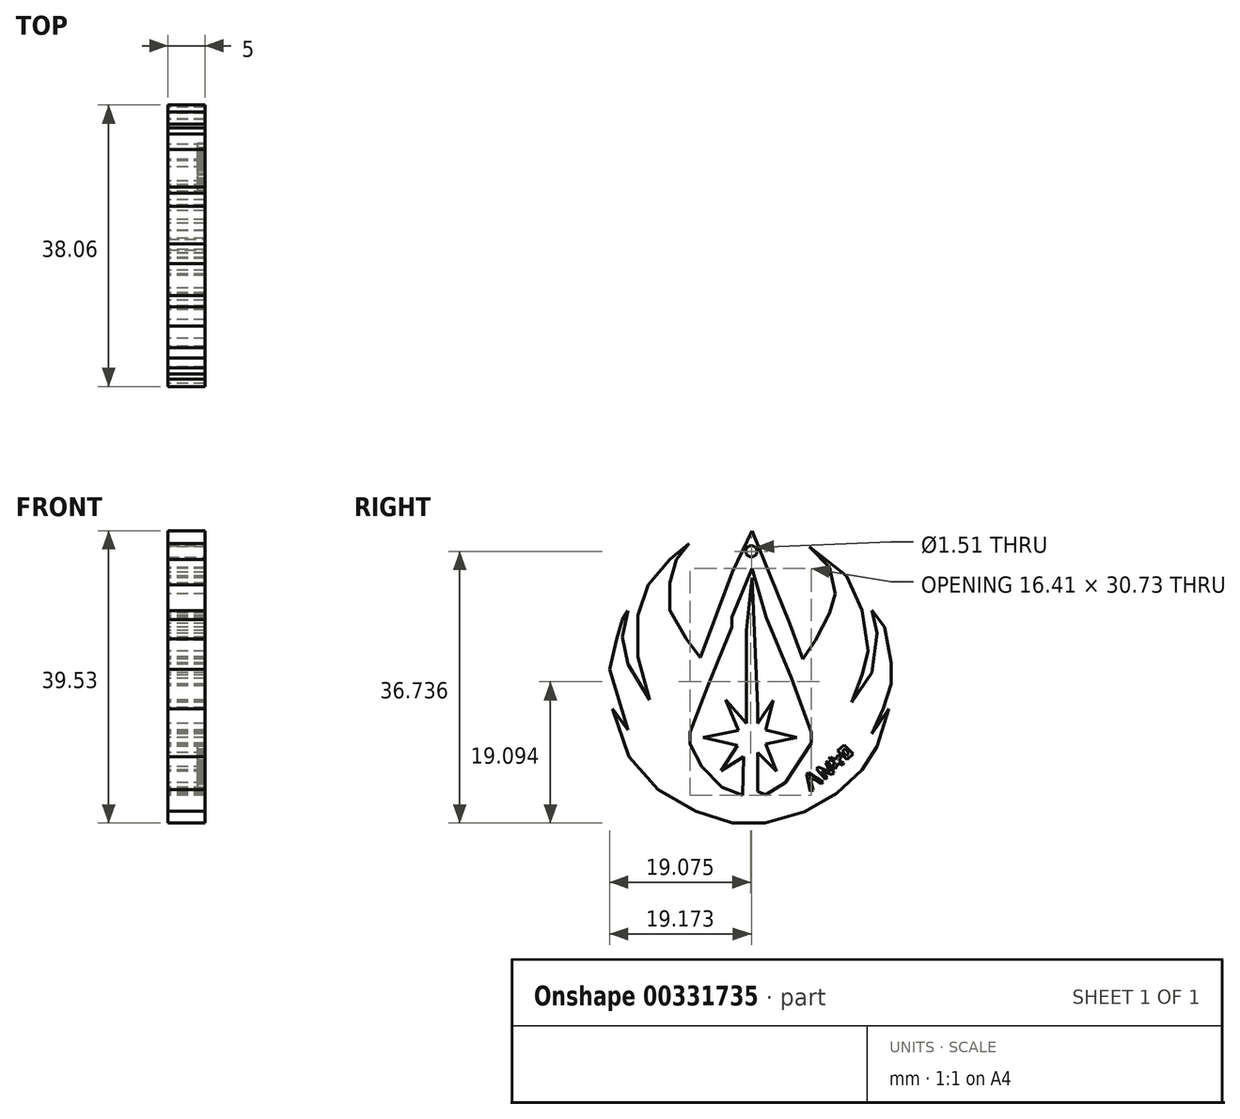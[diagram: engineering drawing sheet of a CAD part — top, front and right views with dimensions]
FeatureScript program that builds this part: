
annotation { "Feature Type Name" : "Feature", "Feature Type Description" : "" }
export const myFeature = defineFeature(function(context is Context, id is Id, definition is map)
    precondition{}
    {
        {
            var Q0;
            Q0=qCreatedBy(makeId("Right.planeOp"),FACE);
            var sketch = newSketch(context, id + "F0", { "sketchPlane" : qUnion([Q0])});
            skLineSegment(sketch, "E0", {"start": v(-23.92, 44.57) * mm, "end": v(-18.84, 32.02) * mm});
            skLineSegment(sketch, "E1", {"start": v(-18.84, 32.02) * mm, "end": v(-17.04, 27.23) * mm});
            skLineSegment(sketch, "E2", {"start": v(-17.04, 27.23) * mm, "end": v(-15.37, 29.74) * mm});
            skLineSegment(sketch, "E3", {"start": v(-15.37, 29.74) * mm, "end": v(-13.45, 33.45) * mm});
            skLineSegment(sketch, "E4", {"start": v(-16.2, 42.4) * mm, "end": v(-13.45, 39.58) * mm});
            skLineSegment(sketch, "E5", {"start": v(-12.67, 36.06) * mm, "end": v(-13.45, 33.45) * mm});
            skLineSegment(sketch, "E6", {"start": v(-12.67, 36.06) * mm, "end": v(-13.45, 39.58) * mm});
            skLineSegment(sketch, "E7", {"start": v(-16.2, 42.4) * mm, "end": v(-11.16, 38.48) * mm});
            skLineSegment(sketch, "E8", {"start": v(-11.16, 38.48) * mm, "end": v(-9.04, 33.84) * mm});
            skLineSegment(sketch, "E9", {"start": v(-9.04, 33.84) * mm, "end": v(-8.24, 28.3) * mm});
            skLineSegment(sketch, "E10", {"start": v(-8.24, 28.3) * mm, "end": v(-9.04, 25.08) * mm});
            skLineSegment(sketch, "E11", {"start": v(-9.04, 25.08) * mm, "end": v(-10.45, 21.36) * mm});
            skLineSegment(sketch, "E12", {"start": v(-10.45, 21.36) * mm, "end": v(-7.73, 25.39) * mm});
            skLineSegment(sketch, "E13", {"start": v(-7.73, 25.39) * mm, "end": v(-7.03, 30.72) * mm});
            skLineSegment(sketch, "E14", {"start": v(-7.03, 30.72) * mm, "end": v(-7.73, 33.84) * mm});
            skLineSegment(sketch, "E15", {"start": v(-7.73, 33.84) * mm, "end": v(-6.02, 31.53) * mm});
            skLineSegment(sketch, "E16", {"start": v(-6.02, 31.53) * mm, "end": v(-5.11, 26.7) * mm});
            skLineSegment(sketch, "E17", {"start": v(-5.11, 26.7) * mm, "end": v(-5.11, 23.87) * mm});
            skLineSegment(sketch, "E18", {"start": v(-5.11, 23.87) * mm, "end": v(-6.22, 20.45) * mm});
            skLineSegment(sketch, "E19", {"start": v(-6.22, 20.45) * mm, "end": v(-7.73, 17.13) * mm});
            skLineSegment(sketch, "E20", {"start": v(-7.73, 17.13) * mm, "end": v(-5.42, 20.45) * mm});
            skLineSegment(sketch, "E21", {"start": v(-5.42, 20.45) * mm, "end": v(-7.04, 15.42) * mm});
            skLineSegment(sketch, "E22", {"start": v(-7.04, 15.42) * mm, "end": v(-9.04, 12.2) * mm});
            skLineSegment(sketch, "E23", {"start": v(-9.04, 12.2) * mm, "end": v(-12.46, 9.07) * mm});
            skLineSegment(sketch, "E24", {"start": v(-12.46, 9.07) * mm, "end": v(-16.8, 6.56) * mm});
            skLineSegment(sketch, "E25", {"start": v(-16.8, 6.56) * mm, "end": v(-22.13, 5.04) * mm});
            skLineSegment(sketch, "E26", {"start": v(-22.13, 5.04) * mm, "end": v(-26.56, 5.04) * mm});
            skLineSegment(sketch, "E27", {"start": v(-26.56, 5.04) * mm, "end": v(-31.5, 6.64) * mm});
            skLineSegment(sketch, "E28", {"start": v(-31.5, 6.64) * mm, "end": v(-36.63, 9.58) * mm});
            skLineSegment(sketch, "E29", {"start": v(-36.63, 9.58) * mm, "end": v(-40.56, 14) * mm});
            skLineSegment(sketch, "E30", {"start": v(-40.56, 14) * mm, "end": v(-42.77, 20.45) * mm});
            skLineSegment(sketch, "E31", {"start": v(-42.77, 20.45) * mm, "end": v(-40.66, 17.63) * mm});
            skLineSegment(sketch, "E32", {"start": v(-40.66, 17.63) * mm, "end": v(-42.17, 22.57) * mm});
            skLineSegment(sketch, "E33", {"start": v(-42.17, 22.57) * mm, "end": v(-43.17, 25.83) * mm});
            skLineSegment(sketch, "E34", {"start": v(-43.17, 25.83) * mm, "end": v(-42.17, 29.92) * mm});
            skLineSegment(sketch, "E35", {"start": v(-41.41, 30.22) * mm, "end": v(-40.66, 26.5) * mm});
            skLineSegment(sketch, "E36", {"start": v(-40.66, 26.5) * mm, "end": v(-37.74, 21.66) * mm});
            skLineSegment(sketch, "E37", {"start": v(-37.74, 21.66) * mm, "end": v(-39.35, 27.5) * mm});
            skLineSegment(sketch, "E38", {"start": v(-39.35, 27.5) * mm, "end": v(-39.35, 33.14) * mm});
            skLineSegment(sketch, "E39", {"start": v(-39.35, 33.14) * mm, "end": v(-37.95, 37.24) * mm});
            skLineSegment(sketch, "E40", {"start": v(-37.95, 37.24) * mm, "end": v(-35.02, 40.7) * mm});
            skLineSegment(sketch, "E41", {"start": v(-35.02, 40.7) * mm, "end": v(-32.4, 42.8) * mm});
            skLineSegment(sketch, "E42", {"start": v(-32.4, 42.8) * mm, "end": v(-34.11, 40.7) * mm});
            skLineSegment(sketch, "E43", {"start": v(-34.11, 40.7) * mm, "end": v(-35.02, 37.47) * mm});
            skLineSegment(sketch, "E44", {"start": v(-35.02, 37.47) * mm, "end": v(-35.02, 33.84) * mm});
            skLineSegment(sketch, "E45", {"start": v(-35.02, 33.84) * mm, "end": v(-32.8, 29.92) * mm});
            skLineSegment(sketch, "E46", {"start": v(-32.8, 29.92) * mm, "end": v(-30.9, 27.4) * mm});
            skLineSegment(sketch, "E47", {"start": v(-30.9, 27.4) * mm, "end": v(-26.56, 38.98) * mm});
            skLineSegment(sketch, "E48", {"start": v(-26.56, 38.98) * mm, "end": v(-23.92, 44.57) * mm});
            skLineSegment(sketch, "E49", {"start": v(-42.17, 29.92) * mm, "end": v(-41.47, 32.53) * mm});
            skLineSegment(sketch, "E50", {"start": v(-41.47, 32.53) * mm, "end": v(-40.66, 33.74) * mm});
            skLineSegment(sketch, "E51", {"start": v(-40.66, 33.74) * mm, "end": v(-41.41, 30.22) * mm});
            skLineSegment(sketch, "E52", {"start": v(-23.94, 38.17) * mm, "end": v(-29.89, 23.57) * mm});
            skLineSegment(sketch, "E53", {"start": v(-29.89, 23.57) * mm, "end": v(-32.3, 17.33) * mm});
            skLineSegment(sketch, "E54", {"start": v(-32.3, 17.33) * mm, "end": v(-32.3, 15.72) * mm});
            skLineSegment(sketch, "E55", {"start": v(-32.3, 15.72) * mm, "end": v(-30.7, 12.7) * mm});
            skLineSegment(sketch, "E56", {"start": v(-30.7, 12.7) * mm, "end": v(-27.97, 9.88) * mm});
            skLineSegment(sketch, "E57", {"start": v(-27.97, 9.88) * mm, "end": v(-25.15, 8.77) * mm});
            skLineSegment(sketch, "E58", {"start": v(-23.14, 9.27) * mm, "end": v(-22.06, 8.84) * mm});
            skLineSegment(sketch, "E59", {"start": v(-22.06, 8.84) * mm, "end": v(-19.41, 10.48) * mm});
            skLineSegment(sketch, "E60", {"start": v(-19.41, 10.48) * mm, "end": v(-15.89, 15.82) * mm});
            skLineSegment(sketch, "E61", {"start": v(-15.89, 15.82) * mm, "end": v(-15.89, 17.33) * mm});
            skLineSegment(sketch, "E62", {"start": v(-15.89, 17.33) * mm, "end": v(-18.6, 24.58) * mm});
            skLineSegment(sketch, "E63", {"start": v(-18.6, 24.58) * mm, "end": v(-22.03, 32.84) * mm});
            skLineSegment(sketch, "E64", {"start": v(-22.03, 32.84) * mm, "end": v(-23.94, 38.17) * mm});
            skLineSegment(sketch, "E65", {"start": v(-23.94, 38.17) * mm, "end": v(-23.92, 44.57) * mm});
            skLineSegment(sketch, "E66", {"start": v(-22.06, 8.84) * mm, "end": v(-22.13, 5.04) * mm});
            skLineSegment(sketch, "E67", {"start": v(-25.15, 8.77) * mm, "end": v(-26.56, 5.04) * mm});
            skLineSegment(sketch, "E68", {"start": v(-23.14, 9.27) * mm, "end": v(-23.14, 14.6) * mm});
            skLineSegment(sketch, "E69", {"start": v(-23.14, 14.6) * mm, "end": v(-20.6, 12.06) * mm});
            skLineSegment(sketch, "E70", {"start": v(-20.6, 12.06) * mm, "end": v(-22.06, 15.7) * mm});
            skLineSegment(sketch, "E71", {"start": v(-22.06, 15.7) * mm, "end": v(-17.9, 16.64) * mm});
            skLineSegment(sketch, "E72", {"start": v(-17.9, 16.64) * mm, "end": v(-22.06, 17.65) * mm});
            skLineSegment(sketch, "E73", {"start": v(-22.06, 17.65) * mm, "end": v(-21.09, 21.64) * mm});
            skLineSegment(sketch, "E74", {"start": v(-21.09, 21.64) * mm, "end": v(-23.14, 18.53) * mm});
            skLineSegment(sketch, "E75", {"start": v(-23.14, 18.53) * mm, "end": v(-23.14, 20.7) * mm});
            skLineSegment(sketch, "E76", {"start": v(-23.14, 20.7) * mm, "end": v(-23.94, 38.17) * mm});
            skLineSegment(sketch, "E77", {"start": v(-23.94, 38.17) * mm, "end": v(-24.67, 31.11) * mm});
            skLineSegment(sketch, "E78", {"start": v(-24.67, 31.11) * mm, "end": v(-24.67, 24.43) * mm});
            skLineSegment(sketch, "E79", {"start": v(-24.67, 24.43) * mm, "end": v(-24.67, 18.5) * mm});
            skLineSegment(sketch, "E80", {"start": v(-24.67, 18.5) * mm, "end": v(-27.47, 21.72) * mm});
            skLineSegment(sketch, "E81", {"start": v(-27.47, 21.72) * mm, "end": v(-25.73, 17.53) * mm});
            skLineSegment(sketch, "E82", {"start": v(-25.73, 17.53) * mm, "end": v(-30.52, 16.64) * mm});
            skLineSegment(sketch, "E83", {"start": v(-30.52, 16.64) * mm, "end": v(-25.86, 15.53) * mm});
            skLineSegment(sketch, "E84", {"start": v(-25.86, 15.53) * mm, "end": v(-28.12, 12.1) * mm});
            skLineSegment(sketch, "E85", {"start": v(-28.12, 12.1) * mm, "end": v(-25.07, 14) * mm});
            skLineSegment(sketch, "E86", {"start": v(-25.07, 14) * mm, "end": v(-25.15, 8.77) * mm});
            skLineSegment(sketch, "E87", {"start": v(-25.07, 14) * mm, "end": v(-23.14, 14.6) * mm});
            skLineSegment(sketch, "E88", {"start": v(-22.03, 32.84) * mm, "end": v(-23.94, 39.5) * mm});
            skLineSegment(sketch, "E89", {"start": v(-23.94, 39.5) * mm, "end": v(-26.65, 32.84) * mm});
            skLineSegment(sketch, "E90", {"start": v(-26.65, 32.84) * mm, "end": v(-26.65, 31.52) * mm});
            skSolve(sketch);
        }
        {
            var Q0;
            Q0=makeQuery(id+"F0.imprint","IMPRINT",FACE,{"disambiguationData":[TD([[makeQuery(id+"F0.imprint","IMPRINT",EDGE,{"derivedFrom":sQuery(id+"F0.wireOp",EDGE,"E0")}),-1.0]])]});
            var Q1;
            Q1=makeQuery(id+"F0.imprint","IMPRINT",FACE,{"disambiguationData":[TD([[makeQuery(id+"F0.imprint","IMPRINT",EDGE,{"derivedFrom":sQuery(id+"F0.wireOp",EDGE,"E27")}),-1.0]])]});
            var Q2;
            Q2=makeQuery(id+"F0.imprint","IMPRINT",FACE,{"disambiguationData":[TD([[makeQuery(id+"F0.imprint","IMPRINT",EDGE,{"derivedFrom":sQuery(id+"F0.wireOp",EDGE,"E26")}),-1.0]])]});
            var Q3;
            Q3=makeQuery(id+"F0.imprint","IMPRINT",FACE,{"disambiguationData":[TD([[makeQuery(id+"F0.imprint","IMPRINT",EDGE,{"derivedFrom":sQuery(id+"F0.wireOp",EDGE,"E69")}),1.0]])]});
            extrude(context, id + "F1", {"entities" : qUnion([Q0, Q1, Q2, Q3]), "depth" : 5 * mm});
        }
        {
            var Q0;
            Q0=makeQuery(id+"F1.opExtrude","CAP_FACE",FACE,{"disambiguationData":[OSD([sQuery(id+"F0.wireOp",EDGE,"E0"),sQuery(id+"F0.wireOp",EDGE,"E1"),sQuery(id+"F0.wireOp",EDGE,"E2"),sQuery(id+"F0.wireOp",EDGE,"E3"),sQuery(id+"F0.wireOp",EDGE,"E4"),sQuery(id+"F0.wireOp",EDGE,"E5"),sQuery(id+"F0.wireOp",EDGE,"E6"),sQuery(id+"F0.wireOp",EDGE,"E7"),sQuery(id+"F0.wireOp",EDGE,"E8"),sQuery(id+"F0.wireOp",EDGE,"E9"),sQuery(id+"F0.wireOp",EDGE,"E10"),sQuery(id+"F0.wireOp",EDGE,"E11"),sQuery(id+"F0.wireOp",EDGE,"E12"),sQuery(id+"F0.wireOp",EDGE,"E13"),sQuery(id+"F0.wireOp",EDGE,"E14"),sQuery(id+"F0.wireOp",EDGE,"E15"),sQuery(id+"F0.wireOp",EDGE,"E16"),sQuery(id+"F0.wireOp",EDGE,"E17"),sQuery(id+"F0.wireOp",EDGE,"E18"),sQuery(id+"F0.wireOp",EDGE,"E19"),sQuery(id+"F0.wireOp",EDGE,"E20"),sQuery(id+"F0.wireOp",EDGE,"E21"),sQuery(id+"F0.wireOp",EDGE,"E22"),sQuery(id+"F0.wireOp",EDGE,"E23"),sQuery(id+"F0.wireOp",EDGE,"E24"),sQuery(id+"F0.wireOp",EDGE,"E25"),sQuery(id+"F0.wireOp",EDGE,"E26"),sQuery(id+"F0.wireOp",EDGE,"E27"),sQuery(id+"F0.wireOp",EDGE,"E28"),sQuery(id+"F0.wireOp",EDGE,"E29"),sQuery(id+"F0.wireOp",EDGE,"E30"),sQuery(id+"F0.wireOp",EDGE,"E31"),sQuery(id+"F0.wireOp",EDGE,"E32"),sQuery(id+"F0.wireOp",EDGE,"E33"),sQuery(id+"F0.wireOp",EDGE,"E34"),sQuery(id+"F0.wireOp",EDGE,"E35"),sQuery(id+"F0.wireOp",EDGE,"E36"),sQuery(id+"F0.wireOp",EDGE,"E37"),sQuery(id+"F0.wireOp",EDGE,"E38"),sQuery(id+"F0.wireOp",EDGE,"E39"),sQuery(id+"F0.wireOp",EDGE,"E40"),sQuery(id+"F0.wireOp",EDGE,"E41"),sQuery(id+"F0.wireOp",EDGE,"E42"),sQuery(id+"F0.wireOp",EDGE,"E43"),sQuery(id+"F0.wireOp",EDGE,"E44"),sQuery(id+"F0.wireOp",EDGE,"E45"),sQuery(id+"F0.wireOp",EDGE,"E46"),sQuery(id+"F0.wireOp",EDGE,"E47"),sQuery(id+"F0.wireOp",EDGE,"E48"),sQuery(id+"F0.wireOp",EDGE,"E49"),sQuery(id+"F0.wireOp",EDGE,"E50"),sQuery(id+"F0.wireOp",EDGE,"E51"),sQuery(id+"F0.wireOp",EDGE,"E52"),sQuery(id+"F0.wireOp",EDGE,"E53"),sQuery(id+"F0.wireOp",EDGE,"E54"),sQuery(id+"F0.wireOp",EDGE,"E55"),sQuery(id+"F0.wireOp",EDGE,"E56"),sQuery(id+"F0.wireOp",EDGE,"E57"),sQuery(id+"F0.wireOp",EDGE,"E58"),sQuery(id+"F0.wireOp",EDGE,"E59"),sQuery(id+"F0.wireOp",EDGE,"E60"),sQuery(id+"F0.wireOp",EDGE,"E61"),sQuery(id+"F0.wireOp",EDGE,"E62"),sQuery(id+"F0.wireOp",EDGE,"E63"),sQuery(id+"F0.wireOp",EDGE,"E68"),sQuery(id+"F0.wireOp",EDGE,"E69"),sQuery(id+"F0.wireOp",EDGE,"E70"),sQuery(id+"F0.wireOp",EDGE,"E71"),sQuery(id+"F0.wireOp",EDGE,"E72"),sQuery(id+"F0.wireOp",EDGE,"E73"),sQuery(id+"F0.wireOp",EDGE,"E74"),sQuery(id+"F0.wireOp",EDGE,"E75"),sQuery(id+"F0.wireOp",EDGE,"E76"),sQuery(id+"F0.wireOp",EDGE,"E77"),sQuery(id+"F0.wireOp",EDGE,"E78"),sQuery(id+"F0.wireOp",EDGE,"E79"),sQuery(id+"F0.wireOp",EDGE,"E80"),sQuery(id+"F0.wireOp",EDGE,"E81"),sQuery(id+"F0.wireOp",EDGE,"E82"),sQuery(id+"F0.wireOp",EDGE,"E83"),sQuery(id+"F0.wireOp",EDGE,"E84"),sQuery(id+"F0.wireOp",EDGE,"E85"),sQuery(id+"F0.wireOp",EDGE,"E86"),sQuery(id+"F0.wireOp",EDGE,"E88"),sQuery(id+"F0.wireOp",EDGE,"E89"),sQuery(id+"F0.wireOp",EDGE,"E90")])],"isStart":false});
            var sketch = newSketch(context, id + "F2", { "sketchPlane" : qUnion([Q0])});
            skCircle(sketch, "E91", {"center": v(-24, 41.78) * mm, "radius": 0.75 * mm});
            skPoint(sketch, "E91.centerSnap0", {"position": v(-25.24, 41.78) * mm});
            skSolve(sketch);
        }
        {
            var Q0;
            Q0=makeQuery(id+"F2.imprint","IMPRINT",FACE,{"disambiguationData":[TD([[makeQuery(id+"F2.imprint","IMPRINT",EDGE,{"derivedFrom":sQuery(id+"F2.wireOp",EDGE,"E91")}),1.0]])]});
            extrude(context, id + "F3", {"entities" : qUnion([Q0]), "operationType" : NewBodyOperationType.REMOVE, "oppositeDirection" : true, "depth" : 5 * mm});
        }
        {
            var Q0;
            Q0=makeQuery(id+"F1.opExtrude","CAP_FACE",FACE,{"disambiguationData":[OSD([sQuery(id+"F0.wireOp",EDGE,"E0"),sQuery(id+"F0.wireOp",EDGE,"E1"),sQuery(id+"F0.wireOp",EDGE,"E2"),sQuery(id+"F0.wireOp",EDGE,"E3"),sQuery(id+"F0.wireOp",EDGE,"E4"),sQuery(id+"F0.wireOp",EDGE,"E5"),sQuery(id+"F0.wireOp",EDGE,"E6"),sQuery(id+"F0.wireOp",EDGE,"E7"),sQuery(id+"F0.wireOp",EDGE,"E8"),sQuery(id+"F0.wireOp",EDGE,"E9"),sQuery(id+"F0.wireOp",EDGE,"E10"),sQuery(id+"F0.wireOp",EDGE,"E11"),sQuery(id+"F0.wireOp",EDGE,"E12"),sQuery(id+"F0.wireOp",EDGE,"E13"),sQuery(id+"F0.wireOp",EDGE,"E14"),sQuery(id+"F0.wireOp",EDGE,"E15"),sQuery(id+"F0.wireOp",EDGE,"E16"),sQuery(id+"F0.wireOp",EDGE,"E17"),sQuery(id+"F0.wireOp",EDGE,"E18"),sQuery(id+"F0.wireOp",EDGE,"E19"),sQuery(id+"F0.wireOp",EDGE,"E20"),sQuery(id+"F0.wireOp",EDGE,"E21"),sQuery(id+"F0.wireOp",EDGE,"E22"),sQuery(id+"F0.wireOp",EDGE,"E23"),sQuery(id+"F0.wireOp",EDGE,"E24"),sQuery(id+"F0.wireOp",EDGE,"E25"),sQuery(id+"F0.wireOp",EDGE,"E26"),sQuery(id+"F0.wireOp",EDGE,"E27"),sQuery(id+"F0.wireOp",EDGE,"E28"),sQuery(id+"F0.wireOp",EDGE,"E29"),sQuery(id+"F0.wireOp",EDGE,"E30"),sQuery(id+"F0.wireOp",EDGE,"E31"),sQuery(id+"F0.wireOp",EDGE,"E32"),sQuery(id+"F0.wireOp",EDGE,"E33"),sQuery(id+"F0.wireOp",EDGE,"E34"),sQuery(id+"F0.wireOp",EDGE,"E35"),sQuery(id+"F0.wireOp",EDGE,"E36"),sQuery(id+"F0.wireOp",EDGE,"E37"),sQuery(id+"F0.wireOp",EDGE,"E38"),sQuery(id+"F0.wireOp",EDGE,"E39"),sQuery(id+"F0.wireOp",EDGE,"E40"),sQuery(id+"F0.wireOp",EDGE,"E41"),sQuery(id+"F0.wireOp",EDGE,"E42"),sQuery(id+"F0.wireOp",EDGE,"E43"),sQuery(id+"F0.wireOp",EDGE,"E44"),sQuery(id+"F0.wireOp",EDGE,"E45"),sQuery(id+"F0.wireOp",EDGE,"E46"),sQuery(id+"F0.wireOp",EDGE,"E47"),sQuery(id+"F0.wireOp",EDGE,"E48"),sQuery(id+"F0.wireOp",EDGE,"E49"),sQuery(id+"F0.wireOp",EDGE,"E50"),sQuery(id+"F0.wireOp",EDGE,"E51"),sQuery(id+"F0.wireOp",EDGE,"E52"),sQuery(id+"F0.wireOp",EDGE,"E53"),sQuery(id+"F0.wireOp",EDGE,"E54"),sQuery(id+"F0.wireOp",EDGE,"E55"),sQuery(id+"F0.wireOp",EDGE,"E56"),sQuery(id+"F0.wireOp",EDGE,"E57"),sQuery(id+"F0.wireOp",EDGE,"E58"),sQuery(id+"F0.wireOp",EDGE,"E59"),sQuery(id+"F0.wireOp",EDGE,"E60"),sQuery(id+"F0.wireOp",EDGE,"E61"),sQuery(id+"F0.wireOp",EDGE,"E62"),sQuery(id+"F0.wireOp",EDGE,"E63"),sQuery(id+"F0.wireOp",EDGE,"E68"),sQuery(id+"F0.wireOp",EDGE,"E69"),sQuery(id+"F0.wireOp",EDGE,"E70"),sQuery(id+"F0.wireOp",EDGE,"E71"),sQuery(id+"F0.wireOp",EDGE,"E72"),sQuery(id+"F0.wireOp",EDGE,"E73"),sQuery(id+"F0.wireOp",EDGE,"E74"),sQuery(id+"F0.wireOp",EDGE,"E75"),sQuery(id+"F0.wireOp",EDGE,"E76"),sQuery(id+"F0.wireOp",EDGE,"E77"),sQuery(id+"F0.wireOp",EDGE,"E78"),sQuery(id+"F0.wireOp",EDGE,"E79"),sQuery(id+"F0.wireOp",EDGE,"E80"),sQuery(id+"F0.wireOp",EDGE,"E81"),sQuery(id+"F0.wireOp",EDGE,"E82"),sQuery(id+"F0.wireOp",EDGE,"E83"),sQuery(id+"F0.wireOp",EDGE,"E84"),sQuery(id+"F0.wireOp",EDGE,"E85"),sQuery(id+"F0.wireOp",EDGE,"E86"),sQuery(id+"F0.wireOp",EDGE,"E88"),sQuery(id+"F0.wireOp",EDGE,"E89"),sQuery(id+"F0.wireOp",EDGE,"E90")])],"isStart":false});
            var sketch = newSketch(context, id + "F4", { "sketchPlane" : qUnion([Q0])});
            skLineSegment(sketch, "E92", {"start": v(-16.03, 9.28) * mm, "end": v(-16.56, 11.65) * mm});
            skLineSegment(sketch, "E93", {"start": v(-16.56, 11.65) * mm, "end": v(-16.3, 11.82) * mm});
            skLineSegment(sketch, "E94", {"start": v(-16.3, 11.82) * mm, "end": v(-14.3, 10.58) * mm});
            skLineSegment(sketch, "E95", {"start": v(-14.3, 10.58) * mm, "end": v(-14.57, 10.34) * mm});
            skLineSegment(sketch, "E96", {"start": v(-14.57, 10.34) * mm, "end": v(-15.6, 11) * mm});
            skLineSegment(sketch, "E97", {"start": v(-15.6, 11) * mm, "end": v(-15.95, 10.72) * mm});
            skLineSegment(sketch, "E98", {"start": v(-15.95, 10.72) * mm, "end": v(-15.67, 9.49) * mm});
            skLineSegment(sketch, "E99", {"start": v(-15.67, 9.49) * mm, "end": v(-16.03, 9.28) * mm});
            skLineSegment(sketch, "E100", {"start": v(-16.06, 10.96) * mm, "end": v(-16.17, 11.26) * mm});
            skLineSegment(sketch, "E101", {"start": v(-16.17, 11.26) * mm, "end": v(-16.02, 11.32) * mm});
            skLineSegment(sketch, "E102", {"start": v(-16.02, 11.32) * mm, "end": v(-15.78, 11.16) * mm});
            skLineSegment(sketch, "E103", {"start": v(-15.78, 11.16) * mm, "end": v(-16.06, 10.96) * mm});
            skLineSegment(sketch, "E104", {"start": v(-14, 10.96) * mm, "end": v(-15.21, 12.33) * mm});
            skLineSegment(sketch, "E105", {"start": v(-14, 10.96) * mm, "end": v(-13.75, 11.2) * mm});
            skLineSegment(sketch, "E106", {"start": v(-13.75, 11.2) * mm, "end": v(-14.52, 12.06) * mm});
            skLineSegment(sketch, "E107", {"start": v(-14.52, 12.06) * mm, "end": v(-13.15, 11.56) * mm});
            skLineSegment(sketch, "E108", {"start": v(-13.15, 11.56) * mm, "end": v(-12.86, 11.76) * mm});
            skLineSegment(sketch, "E109", {"start": v(-12.86, 11.76) * mm, "end": v(-13.65, 13.4) * mm});
            skLineSegment(sketch, "E110", {"start": v(-15.21, 12.33) * mm, "end": v(-14.94, 12.58) * mm});
            skLineSegment(sketch, "E111", {"start": v(-13.38, 12) * mm, "end": v(-14.94, 12.58) * mm});
            skLineSegment(sketch, "E112", {"start": v(-13.65, 13.4) * mm, "end": v(-13.95, 13.2) * mm});
            skLineSegment(sketch, "E113", {"start": v(-13.95, 13.2) * mm, "end": v(-13.38, 12) * mm});
            skLineSegment(sketch, "E114", {"start": v(-13.47, 13.61) * mm, "end": v(-11.67, 12.84) * mm});
            skLineSegment(sketch, "E115", {"start": v(-11.67, 12.84) * mm, "end": v(-11.53, 13.17) * mm});
            skLineSegment(sketch, "E116", {"start": v(-11.53, 13.17) * mm, "end": v(-13.32, 13.93) * mm});
            skLineSegment(sketch, "E117", {"start": v(-13.32, 13.93) * mm, "end": v(-13.47, 13.61) * mm});
            skLineSegment(sketch, "E118", {"start": v(-12.66, 12.38) * mm, "end": v(-13.03, 12.58) * mm});
            skLineSegment(sketch, "E119", {"start": v(-12.33, 14.84) * mm, "end": v(-11.07, 13.6) * mm});
            skLineSegment(sketch, "E120", {"start": v(-11.07, 13.6) * mm, "end": v(-10.27, 14.4) * mm});
            skLineSegment(sketch, "E121", {"start": v(-10.27, 14.4) * mm, "end": v(-11.46, 15.57) * mm});
            skLineSegment(sketch, "E122", {"start": v(-11.46, 15.57) * mm, "end": v(-12.33, 14.84) * mm});
            skLineSegment(sketch, "E123", {"start": v(-11.37, 15.05) * mm, "end": v(-10.8, 14.48) * mm});
            skLineSegment(sketch, "E124", {"start": v(-10.8, 14.48) * mm, "end": v(-11.18, 14.1) * mm});
            skLineSegment(sketch, "E125", {"start": v(-11.18, 14.1) * mm, "end": v(-11.74, 14.68) * mm});
            skLineSegment(sketch, "E126", {"start": v(-11.74, 14.68) * mm, "end": v(-11.37, 15.05) * mm});
            skLineSegment(sketch, "E127", {"start": v(-13.03, 12.58) * mm, "end": v(-12.31, 14.28) * mm});
            skLineSegment(sketch, "E128", {"start": v(-12.31, 14.28) * mm, "end": v(-11.88, 14.1) * mm});
            skLineSegment(sketch, "E129", {"start": v(-11.88, 14.1) * mm, "end": v(-12.66, 12.38) * mm});
            skSolve(sketch);
        }
        {
            var Q0;
            Q0=makeQuery(id+"F4.imprint","IMPRINT",FACE,{"disambiguationData":[TD([[makeQuery(id+"F4.imprint","IMPRINT",EDGE,{"derivedFrom":sQuery(id+"F4.wireOp",EDGE,"E104")}),-1.0]])]});
            var Q1;
            {var subQ0=sQuery(id+"F4.wireOp",EDGE,"E117");Q1=makeQuery(id+"F4.imprint","IMPRINT",FACE,{"disambiguationData":[TD([[makeQuery(id+"F4.imprint","IMPRINT",EDGE,{"derivedFrom":subQ0}),1.0]])]});}
            var Q2;
            {var subQ5=sQuery(id+"F4.wireOp",EDGE,"E118");Q2=makeQuery(id+"F4.imprint","IMPRINT",FACE,{"disambiguationData":[TD([[makeQuery(id+"F4.imprint","IMPRINT",EDGE,{"derivedFrom":subQ5}),-1.0]])]});}
            var Q3;
            {var subQ0=sQuery(id+"F4.wireOp",EDGE,"E115");Q3=makeQuery(id+"F4.imprint","IMPRINT",FACE,{"disambiguationData":[TD([[makeQuery(id+"F4.imprint","IMPRINT",EDGE,{"derivedFrom":subQ0}),1.0]])]});}
            var Q4;
            {var subQ5=sQuery(id+"F4.wireOp",EDGE,"UI4K8p10-bpox-CDKy-jhsV-qxIdmNQmzXu3");Q4=makeQuery(id+"F4.imprint","IMPRINT",FACE,{"disambiguationData":[TD([[makeQuery(id+"F4.imprint","IMPRINT",EDGE,{"derivedFrom":subQ5}),-1.0]])]});}
            var Q5;
            Q5=makeQuery(id+"F4.imprint","IMPRINT",FACE,{"disambiguationData":[TD([[makeQuery(id+"F4.imprint","IMPRINT",EDGE,{"derivedFrom":sQuery(id+"F4.wireOp",EDGE,"E119")}),1.0]])]});
            var Q6;
            {var subQ0=sQuery(id+"F4.wireOp",EDGE,"EP2ONTnc-Ei56-w7ha-3F1x-Jlb20oOLGOqn");var subQ1=sQuery(id+"F4.wireOp",EDGE,"E114");var subQ2=makeQuery(id+"F4.imprint","INTERSECT",VERTEX,{"derivedFrom":[subQ1,subQ0]});Q6=makeQuery(id+"F4.imprint","IMPRINT",FACE,{"disambiguationData":[TD([[makeQuery(id+"F4.imprint","IMPRINT",EDGE,{"disambiguationData":[TD([[subQ2,-1.0]])],"derivedFrom":subQ1}),1.0]])]});}
            var Q7;
            Q7=makeQuery(id+"F4.imprint","IMPRINT",FACE,{"disambiguationData":[TD([[makeQuery(id+"F4.imprint","IMPRINT",EDGE,{"derivedFrom":sQuery(id+"F4.wireOp",EDGE,"E92")}),-1.0]])]});
            var Q8;
            {var subQ5=sQuery(id+"F4.wireOp",EDGE,"E128");Q8=makeQuery(id+"F4.imprint","IMPRINT",FACE,{"disambiguationData":[TD([[makeQuery(id+"F4.imprint","IMPRINT",EDGE,{"derivedFrom":subQ5}),-1.0]])]});}
            extrude(context, id + "F5", {"entities" : qUnion([Q0, Q1, Q2, Q3, Q4, Q5, Q6, Q7, Q8]), "operationType" : NewBodyOperationType.REMOVE, "oppositeDirection" : true, "depth" : 1 * mm});
        }
    });
